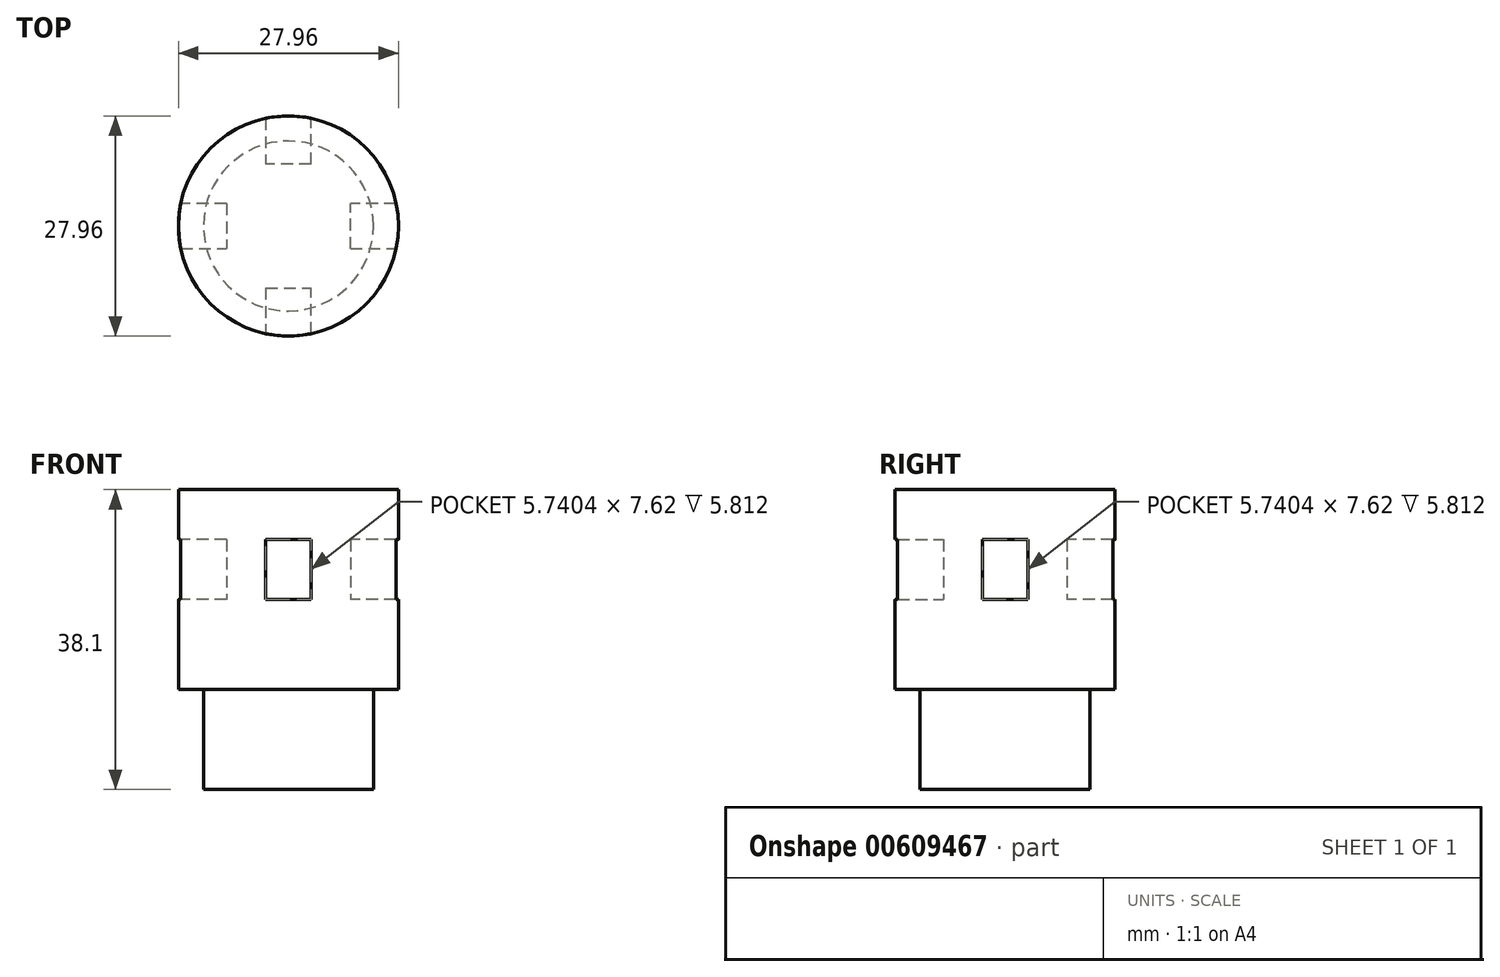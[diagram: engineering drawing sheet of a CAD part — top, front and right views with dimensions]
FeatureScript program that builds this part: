
annotation { "Feature Type Name" : "Feature", "Feature Type Description" : "" }
export const myFeature = defineFeature(function(context is Context, id is Id, definition is map)
    precondition{}
    {
        {
            var Q0;
            Q0=qCreatedBy(makeId("Top.planeOp"),FACE);
            var sketch = newSketch(context, id + "F0", { "sketchPlane" : qUnion([Q0])});
            skCircle(sketch, "E0", {"center": v(0, 0) * mm, "radius": 13.98 * mm});
            skCircle(sketch, "E1", {"center": v(0, 0) * mm, "radius": 10.8 * mm});
            skLineSegment(sketch, "E2", {"start": v(0, 13.98) * mm, "end": v(-2.87, 13.98) * mm});
            skLineSegment(sketch, "E3", {"start": v(0, 13.98) * mm, "end": v(2.87, 13.98) * mm});
            skLineSegment(sketch, "E4", {"start": v(-2.87, 13.98) * mm, "end": v(-2.87, 10.4) * mm});
            skLineSegment(sketch, "E5", {"start": v(-2.87, 10.4) * mm, "end": v(2.87, 10.4) * mm});
            skLineSegment(sketch, "E6", {"start": v(2.87, 10.4) * mm, "end": v(2.87, 13.98) * mm});
            skLineSegment(sketch, "E7.1.0", {"start": v(-13.98, -2.87) * mm, "end": v(-10.4, -2.87) * mm});
            skLineSegment(sketch, "E7.1.1", {"start": v(-13.98, 0) * mm, "end": v(-13.98, -2.87) * mm});
            skLineSegment(sketch, "E7.1.2", {"start": v(-13.98, 0) * mm, "end": v(-13.98, 2.87) * mm});
            skLineSegment(sketch, "E7.1.3", {"start": v(-10.4, -2.87) * mm, "end": v(-10.4, 2.87) * mm});
            skLineSegment(sketch, "E7.1.4", {"start": v(-10.4, 2.87) * mm, "end": v(-13.98, 2.87) * mm});
            skLineSegment(sketch, "E7.2.0", {"start": v(2.87, -13.98) * mm, "end": v(2.87, -10.4) * mm});
            skLineSegment(sketch, "E7.2.1", {"start": v(0, -13.98) * mm, "end": v(2.87, -13.98) * mm});
            skLineSegment(sketch, "E7.2.2", {"start": v(0, -13.98) * mm, "end": v(-2.87, -13.98) * mm});
            skLineSegment(sketch, "E7.2.3", {"start": v(2.87, -10.4) * mm, "end": v(-2.87, -10.4) * mm});
            skLineSegment(sketch, "E7.2.4", {"start": v(-2.87, -10.4) * mm, "end": v(-2.87, -13.98) * mm});
            skLineSegment(sketch, "E7.3.0", {"start": v(13.98, 2.87) * mm, "end": v(10.4, 2.87) * mm});
            skLineSegment(sketch, "E7.3.1", {"start": v(13.98, 0) * mm, "end": v(13.98, 2.87) * mm});
            skLineSegment(sketch, "E7.3.2", {"start": v(13.98, 0) * mm, "end": v(13.98, -2.87) * mm});
            skLineSegment(sketch, "E7.3.3", {"start": v(10.4, 2.87) * mm, "end": v(10.4, -2.87) * mm});
            skLineSegment(sketch, "E7.3.4", {"start": v(10.4, -2.87) * mm, "end": v(13.98, -2.87) * mm});
            skLineSegment(sketch, "E8", {"start": v(10.4, -2.87) * mm, "end": v(7.87, -2.87) * mm});
            skLineSegment(sketch, "E9", {"start": v(7.87, -2.87) * mm, "end": v(7.87, 2.87) * mm});
            skLineSegment(sketch, "E10", {"start": v(7.87, 2.87) * mm, "end": v(10.4, 2.87) * mm});
            skLineSegment(sketch, "E11.1.0", {"start": v(2.87, 7.87) * mm, "end": v(-2.87, 7.87) * mm});
            skLineSegment(sketch, "E11.1.1", {"start": v(-2.87, 7.87) * mm, "end": v(-2.87, 10.4) * mm});
            skLineSegment(sketch, "E11.1.2", {"start": v(2.87, 10.4) * mm, "end": v(2.87, 7.87) * mm});
            skLineSegment(sketch, "E11.2.0", {"start": v(-7.87, 2.87) * mm, "end": v(-7.87, -2.87) * mm});
            skLineSegment(sketch, "E11.2.1", {"start": v(-7.87, -2.87) * mm, "end": v(-10.4, -2.87) * mm});
            skLineSegment(sketch, "E11.2.2", {"start": v(-10.4, 2.87) * mm, "end": v(-7.87, 2.87) * mm});
            skLineSegment(sketch, "E11.3.0", {"start": v(-2.87, -7.87) * mm, "end": v(2.87, -7.87) * mm});
            skLineSegment(sketch, "E11.3.1", {"start": v(2.87, -7.87) * mm, "end": v(2.87, -10.4) * mm});
            skLineSegment(sketch, "E11.3.2", {"start": v(-2.87, -10.4) * mm, "end": v(-2.87, -7.87) * mm});
            skSolve(sketch);
        }
        {
            var Q0;
            {var subQ0=sQuery(id+"F0.wireOp",EDGE,"E4");var subQ1=sQuery(id+"F0.wireOp",EDGE,"E0");var subQ2=makeQuery(id+"F0.imprint","INTERSECT",VERTEX,{"derivedFrom":[subQ1,subQ0]});Q0=makeQuery(id+"F0.imprint","IMPRINT",FACE,{"disambiguationData":[TD([[makeQuery(id+"F0.imprint","IMPRINT",EDGE,{"disambiguationData":[TD([[subQ2,-1.0]])],"derivedFrom":subQ1}),1.0]])]});}
            var Q1;
            {var subQ0=sQuery(id+"F0.wireOp",EDGE,"E5");Q1=makeQuery(id+"F0.imprint","IMPRINT",FACE,{"disambiguationData":[TD([[makeQuery(id+"F0.imprint","IMPRINT",EDGE,{"derivedFrom":subQ0}),1.0]])]});}
            var Q2;
            {var subQ4=sQuery(id+"F0.wireOp",EDGE,"E0");var subQ6=sQuery(id+"F0.wireOp",EDGE,"E6");var subQ9=makeQuery(id+"F0.imprint","INTERSECT",VERTEX,{"derivedFrom":[subQ4,subQ6]});Q2=makeQuery(id+"F0.imprint","IMPRINT",FACE,{"disambiguationData":[TD([[makeQuery(id+"F0.imprint","IMPRINT",EDGE,{"disambiguationData":[TD([[subQ9,-1.0]])],"derivedFrom":subQ4}),1.0]])]});}
            var Q3;
            {var subQ0=sQuery(id+"F0.wireOp",EDGE,"E7.3.0");var subQ1=sQuery(id+"F0.wireOp",EDGE,"E0");var subQ2=makeQuery(id+"F0.imprint","INTERSECT",VERTEX,{"derivedFrom":[subQ1,subQ0]});Q3=makeQuery(id+"F0.imprint","IMPRINT",FACE,{"disambiguationData":[TD([[makeQuery(id+"F0.imprint","IMPRINT",EDGE,{"disambiguationData":[TD([[subQ2,-1.0]])],"derivedFrom":subQ1}),1.0]])]});}
            var Q4;
            {var subQ1=sQuery(id+"F0.wireOp",EDGE,"E7.3.0");var subQ4=sQuery(id+"F0.wireOp",EDGE,"E0");var subQ5=makeQuery(id+"F0.imprint","INTERSECT",VERTEX,{"derivedFrom":[subQ4,subQ1]});Q4=makeQuery(id+"F0.imprint","IMPRINT",FACE,{"disambiguationData":[TD([[makeQuery(id+"F0.imprint","IMPRINT",EDGE,{"disambiguationData":[TD([[subQ5,1.0]])],"derivedFrom":subQ4}),1.0]])]});}
            var Q5;
            {var subQ4=sQuery(id+"F0.wireOp",EDGE,"E5");Q5=makeQuery(id+"F0.imprint","IMPRINT",FACE,{"disambiguationData":[TD([[makeQuery(id+"F0.imprint","IMPRINT",EDGE,{"derivedFrom":subQ4}),-1.0]])]});}
            var Q6;
            {var subQ0=sQuery(id+"F0.wireOp",EDGE,"E7.3.3");Q6=makeQuery(id+"F0.imprint","IMPRINT",FACE,{"disambiguationData":[TD([[makeQuery(id+"F0.imprint","IMPRINT",EDGE,{"derivedFrom":subQ0}),1.0]])]});}
            var Q7;
            {var subQ0=sQuery(id+"F0.wireOp",EDGE,"E7.2.0");var subQ1=sQuery(id+"F0.wireOp",EDGE,"E0");var subQ2=makeQuery(id+"F0.imprint","INTERSECT",VERTEX,{"derivedFrom":[subQ1,subQ0]});Q7=makeQuery(id+"F0.imprint","IMPRINT",FACE,{"disambiguationData":[TD([[makeQuery(id+"F0.imprint","IMPRINT",EDGE,{"disambiguationData":[TD([[subQ2,-1.0]])],"derivedFrom":subQ1}),1.0]])]});}
            var Q8;
            {var subQ0=sQuery(id+"F0.wireOp",EDGE,"E7.1.0");var subQ1=sQuery(id+"F0.wireOp",EDGE,"E0");var subQ2=makeQuery(id+"F0.imprint","INTERSECT",VERTEX,{"derivedFrom":[subQ1,subQ0]});Q8=makeQuery(id+"F0.imprint","IMPRINT",FACE,{"disambiguationData":[TD([[makeQuery(id+"F0.imprint","IMPRINT",EDGE,{"disambiguationData":[TD([[subQ2,-1.0]])],"derivedFrom":subQ1}),1.0]])]});}
            var Q9;
            {var subQ4=sQuery(id+"F0.wireOp",EDGE,"E0");var subQ7=sQuery(id+"F0.wireOp",EDGE,"E7.1.4");var subQ9=makeQuery(id+"F0.imprint","INTERSECT",VERTEX,{"derivedFrom":[subQ4,subQ7]});Q9=makeQuery(id+"F0.imprint","IMPRINT",FACE,{"disambiguationData":[TD([[makeQuery(id+"F0.imprint","IMPRINT",EDGE,{"disambiguationData":[TD([[subQ9,-1.0]])],"derivedFrom":subQ4}),1.0]])]});}
            var Q10;
            {var subQ0=sQuery(id+"F0.wireOp",EDGE,"E7.1.3");Q10=makeQuery(id+"F0.imprint","IMPRINT",FACE,{"disambiguationData":[TD([[makeQuery(id+"F0.imprint","IMPRINT",EDGE,{"derivedFrom":subQ0}),1.0]])]});}
            var Q11;
            {var subQ4=sQuery(id+"F0.wireOp",EDGE,"E0");var subQ6=sQuery(id+"F0.wireOp",EDGE,"E7.2.4");var subQ8=makeQuery(id+"F0.imprint","INTERSECT",VERTEX,{"derivedFrom":[subQ4,subQ6]});Q11=makeQuery(id+"F0.imprint","IMPRINT",FACE,{"disambiguationData":[TD([[makeQuery(id+"F0.imprint","IMPRINT",EDGE,{"disambiguationData":[TD([[subQ8,-1.0]])],"derivedFrom":subQ4}),1.0]])]});}
            var Q12;
            {var subQ0=sQuery(id+"F0.wireOp",EDGE,"E7.2.3");Q12=makeQuery(id+"F0.imprint","IMPRINT",FACE,{"disambiguationData":[TD([[makeQuery(id+"F0.imprint","IMPRINT",EDGE,{"derivedFrom":subQ0}),1.0]])]});}
            var Q13;
            Q13=makeQuery(id+"F0.imprint","IMPRINT",FACE,{"disambiguationData":[TD([[makeQuery(id+"F0.imprint","IMPRINT",EDGE,{"derivedFrom":sQuery(id+"F0.wireOp",EDGE,"E7.1.3")}),-1.0]])]});
            var Q14;
            {var subQ3=sQuery(id+"F0.wireOp",EDGE,"E8");Q14=makeQuery(id+"F0.imprint","IMPRINT",FACE,{"disambiguationData":[TD([[makeQuery(id+"F0.imprint","IMPRINT",EDGE,{"derivedFrom":subQ3}),1.0]])]});}
            var Q15;
            Q15=makeQuery(id+"F0.imprint","IMPRINT",FACE,{"disambiguationData":[TD([[makeQuery(id+"F0.imprint","IMPRINT",EDGE,{"derivedFrom":sQuery(id+"F0.wireOp",EDGE,"E7.3.3")}),-1.0]])]});
            var Q16;
            Q16=makeQuery(id+"F0.imprint","IMPRINT",FACE,{"disambiguationData":[TD([[makeQuery(id+"F0.imprint","IMPRINT",EDGE,{"derivedFrom":sQuery(id+"F0.wireOp",EDGE,"E7.2.3")}),-1.0]])]});
            extrude(context, id + "F1", {"entities" : qUnion([Q0, Q1, Q2, Q3, Q4, Q5, Q6, Q7, Q8, Q9, Q10, Q11, Q12, Q13, Q14, Q15, Q16]), "depth" : 25.4 * mm, "offsetDistance" : 25.4 * mm});
        }
        {
            var Q0;
            {var subQ4=sQuery(id+"F0.wireOp",EDGE,"E0");var subQ7=sQuery(id+"F0.wireOp",EDGE,"E7.1.4");var subQ9=makeQuery(id+"F0.imprint","INTERSECT",VERTEX,{"derivedFrom":[subQ4,subQ7]});Q0=makeQuery(id+"F0.imprint","IMPRINT",FACE,{"disambiguationData":[TD([[makeQuery(id+"F0.imprint","IMPRINT",EDGE,{"disambiguationData":[TD([[subQ9,-1.0]])],"derivedFrom":subQ4}),1.0]])]});}
            var Q1;
            {var subQ0=sQuery(id+"F0.wireOp",EDGE,"E7.1.3");Q1=makeQuery(id+"F0.imprint","IMPRINT",FACE,{"disambiguationData":[TD([[makeQuery(id+"F0.imprint","IMPRINT",EDGE,{"derivedFrom":subQ0}),1.0]])]});}
            var Q2;
            {var subQ4=sQuery(id+"F0.wireOp",EDGE,"E0");var subQ6=sQuery(id+"F0.wireOp",EDGE,"E7.2.4");var subQ8=makeQuery(id+"F0.imprint","INTERSECT",VERTEX,{"derivedFrom":[subQ4,subQ6]});Q2=makeQuery(id+"F0.imprint","IMPRINT",FACE,{"disambiguationData":[TD([[makeQuery(id+"F0.imprint","IMPRINT",EDGE,{"disambiguationData":[TD([[subQ8,-1.0]])],"derivedFrom":subQ4}),1.0]])]});}
            var Q3;
            {var subQ0=sQuery(id+"F0.wireOp",EDGE,"E7.2.3");Q3=makeQuery(id+"F0.imprint","IMPRINT",FACE,{"disambiguationData":[TD([[makeQuery(id+"F0.imprint","IMPRINT",EDGE,{"derivedFrom":subQ0}),1.0]])]});}
            var Q4;
            {var subQ4=sQuery(id+"F0.wireOp",EDGE,"E0");var subQ6=sQuery(id+"F0.wireOp",EDGE,"E6");var subQ9=makeQuery(id+"F0.imprint","INTERSECT",VERTEX,{"derivedFrom":[subQ4,subQ6]});Q4=makeQuery(id+"F0.imprint","IMPRINT",FACE,{"disambiguationData":[TD([[makeQuery(id+"F0.imprint","IMPRINT",EDGE,{"disambiguationData":[TD([[subQ9,-1.0]])],"derivedFrom":subQ4}),1.0]])]});}
            var Q5;
            {var subQ0=sQuery(id+"F0.wireOp",EDGE,"E5");Q5=makeQuery(id+"F0.imprint","IMPRINT",FACE,{"disambiguationData":[TD([[makeQuery(id+"F0.imprint","IMPRINT",EDGE,{"derivedFrom":subQ0}),1.0]])]});}
            var Q6;
            {var subQ0=sQuery(id+"F0.wireOp",EDGE,"E7.3.3");Q6=makeQuery(id+"F0.imprint","IMPRINT",FACE,{"disambiguationData":[TD([[makeQuery(id+"F0.imprint","IMPRINT",EDGE,{"derivedFrom":subQ0}),1.0]])]});}
            var Q7;
            {var subQ1=sQuery(id+"F0.wireOp",EDGE,"E7.3.0");var subQ4=sQuery(id+"F0.wireOp",EDGE,"E0");var subQ5=makeQuery(id+"F0.imprint","INTERSECT",VERTEX,{"derivedFrom":[subQ4,subQ1]});Q7=makeQuery(id+"F0.imprint","IMPRINT",FACE,{"disambiguationData":[TD([[makeQuery(id+"F0.imprint","IMPRINT",EDGE,{"disambiguationData":[TD([[subQ5,1.0]])],"derivedFrom":subQ4}),1.0]])]});}
            var Q8;
            Q8=makeQuery(id+"F0.imprint","IMPRINT",FACE,{"disambiguationData":[TD([[makeQuery(id+"F0.imprint","IMPRINT",EDGE,{"derivedFrom":sQuery(id+"F0.wireOp",EDGE,"E7.1.3")}),-1.0]])]});
            var Q9;
            Q9=makeQuery(id+"F0.imprint","IMPRINT",FACE,{"disambiguationData":[TD([[makeQuery(id+"F0.imprint","IMPRINT",EDGE,{"derivedFrom":sQuery(id+"F0.wireOp",EDGE,"E5")}),-1.0]])]});
            var Q10;
            Q10=makeQuery(id+"F0.imprint","IMPRINT",FACE,{"disambiguationData":[TD([[makeQuery(id+"F0.imprint","IMPRINT",EDGE,{"derivedFrom":sQuery(id+"F0.wireOp",EDGE,"E7.3.3")}),-1.0]])]});
            var Q11;
            Q11=makeQuery(id+"F0.imprint","IMPRINT",FACE,{"disambiguationData":[TD([[makeQuery(id+"F0.imprint","IMPRINT",EDGE,{"derivedFrom":sQuery(id+"F0.wireOp",EDGE,"E7.2.3")}),-1.0]])]});
            extrude(context, id + "F2", {"entities" : qUnion([Q0, Q1, Q2, Q3, Q4, Q5, Q6, Q7, Q8, Q9, Q10, Q11]), "operationType" : NewBodyOperationType.REMOVE, "depth" : 19.05 * mm, "offsetDistance" : 25.4 * mm, "hasSecondDirection" : true, "secondDirectionOppositeDirection" : false, "secondDirectionDepth" : 11.43 * mm});
        }
        {
            var Q0;
            {var subQ4=sQuery(id+"F0.wireOp",EDGE,"E5");Q0=makeQuery(id+"F0.imprint","IMPRINT",FACE,{"disambiguationData":[TD([[makeQuery(id+"F0.imprint","IMPRINT",EDGE,{"derivedFrom":subQ4}),-1.0]])]});}
            var Q1;
            {var subQ0=sQuery(id+"F0.wireOp",EDGE,"E7.1.3");Q1=makeQuery(id+"F0.imprint","IMPRINT",FACE,{"disambiguationData":[TD([[makeQuery(id+"F0.imprint","IMPRINT",EDGE,{"derivedFrom":subQ0}),1.0]])]});}
            var Q2;
            {var subQ0=sQuery(id+"F0.wireOp",EDGE,"E7.2.3");Q2=makeQuery(id+"F0.imprint","IMPRINT",FACE,{"disambiguationData":[TD([[makeQuery(id+"F0.imprint","IMPRINT",EDGE,{"derivedFrom":subQ0}),1.0]])]});}
            var Q3;
            {var subQ0=sQuery(id+"F0.wireOp",EDGE,"E5");Q3=makeQuery(id+"F0.imprint","IMPRINT",FACE,{"disambiguationData":[TD([[makeQuery(id+"F0.imprint","IMPRINT",EDGE,{"derivedFrom":subQ0}),1.0]])]});}
            var Q4;
            {var subQ0=sQuery(id+"F0.wireOp",EDGE,"E7.3.3");Q4=makeQuery(id+"F0.imprint","IMPRINT",FACE,{"disambiguationData":[TD([[makeQuery(id+"F0.imprint","IMPRINT",EDGE,{"derivedFrom":subQ0}),1.0]])]});}
            var Q5;
            {var subQ3=sQuery(id+"F0.wireOp",EDGE,"E8");Q5=makeQuery(id+"F0.imprint","IMPRINT",FACE,{"disambiguationData":[TD([[makeQuery(id+"F0.imprint","IMPRINT",EDGE,{"derivedFrom":subQ3}),1.0]])]});}
            var Q6;
            Q6=makeQuery(id+"F0.imprint","IMPRINT",FACE,{"disambiguationData":[TD([[makeQuery(id+"F0.imprint","IMPRINT",EDGE,{"derivedFrom":sQuery(id+"F0.wireOp",EDGE,"E7.2.3")}),-1.0]])]});
            var Q7;
            Q7=makeQuery(id+"F0.imprint","IMPRINT",FACE,{"disambiguationData":[TD([[makeQuery(id+"F0.imprint","IMPRINT",EDGE,{"derivedFrom":sQuery(id+"F0.wireOp",EDGE,"E7.1.3")}),-1.0]])]});
            var Q8;
            Q8=makeQuery(id+"F0.imprint","IMPRINT",FACE,{"disambiguationData":[TD([[makeQuery(id+"F0.imprint","IMPRINT",EDGE,{"derivedFrom":sQuery(id+"F0.wireOp",EDGE,"E7.3.3")}),-1.0]])]});
            extrude(context, id + "F3", {"entities" : qUnion([Q0, Q1, Q2, Q3, Q4, Q5, Q6, Q7, Q8]), "oppositeDirection" : true, "depth" : 12.7 * mm, "offsetDistance" : 25.4 * mm});
        }
    });
